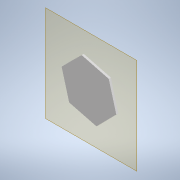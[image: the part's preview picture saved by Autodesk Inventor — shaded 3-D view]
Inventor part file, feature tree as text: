
AUTODESK INVENTOR PART (.ipt)
format: ipt  version: 2020 (Build 240168000, 168)  size: 120,832 bytes
history: native  units: in
note: dims shown in document units (in); Inventor stores cm internally (conversion verified against a paired STEP export)
features: other x3, plane x1, extrude x1, sketch x1
ambient origin geometry x8: Origin, YZ Plane, XZ Plane, XY Plane, X Axis, Y Axis, Z Axis, Center Point
bodies: Solid1 (feature_tree)
feature tree (6):
  plane  "Work Plane1"
  extrude  "Extrusion1"  Depth=1.0in
  sketch  "Sketch1"  dims[d0=6.874in d1=0.0033in d2=13.882in d3=2.3622in d5=360.0deg d7=1.0in d8=0.0in]
  other  "<userpath>\Documents\inventor\md\Project\Assembly2.iam"
  other  "Assembly2.iam"
  other  "Part6:2"
